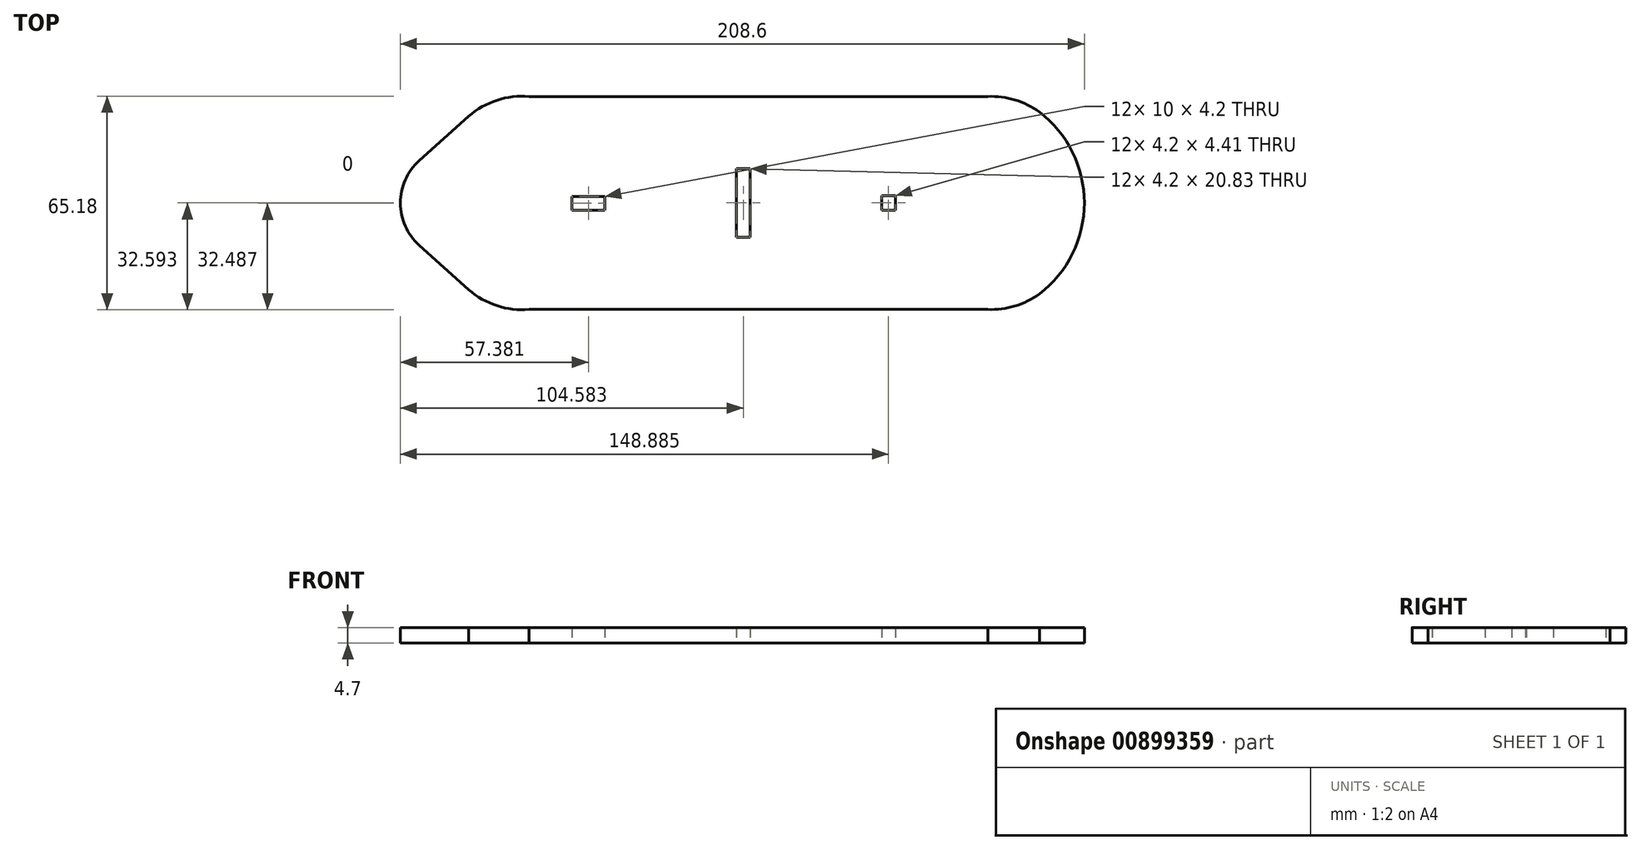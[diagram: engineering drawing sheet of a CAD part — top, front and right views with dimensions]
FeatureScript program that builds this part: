
annotation { "Feature Type Name" : "Feature", "Feature Type Description" : "" }
export const myFeature = defineFeature(function(context is Context, id is Id, definition is map)
    precondition{}
    {
        {
            var Q0;
            Q0=qCreatedBy(makeId("Top.planeOp"),FACE);
            var sketch = newSketch(context, id + "F0", { "sketchPlane" : qUnion([Q0])});
            skArc(sketch, "E0.8", {"start": v(94.32, -610.25) * mm, "mid": v(78.14, -618.43) * mm, "end": v(60.17, -620.91) * mm});
            skLineSegment(sketch, "E0.9", {"start": v(-78.18, -620.91) * mm, "end": v(60.17, -620.91) * mm});
            skPoint(sketch, "E1.middle", {"position": v(-6.1, 79.7) * mm});
            skPoint(sketch, "E2.endSnap0", {"position": v(-81.1, 79.7) * mm});
            skPoint(sketch, "E3", {"position": v(-9.8, 79.7) * mm});
            skPoint(sketch, "E4.orphan", {"position": v(-100.53, 79.7) * mm});
            skPoint(sketch, "E5", {"position": v(-57, 79.6) * mm});
            skPoint(sketch, "E6", {"position": v(34.7, 79.7) * mm});
            skLineSegment(sketch, "E7.bottom", {"start": v(-62, 81.7) * mm, "end": v(-52, 81.7) * mm});
            skLineSegment(sketch, "E7.top", {"start": v(-62, 77.5) * mm, "end": v(-52, 77.5) * mm});
            skLineSegment(sketch, "E7.left", {"start": v(-62, 81.7) * mm, "end": v(-62, 77.5) * mm});
            skLineSegment(sketch, "E7.right", {"start": v(-52, 81.7) * mm, "end": v(-52, 77.5) * mm});
            skLineSegment(sketch, "E8.MirrorCS", {"start": v(32.4, 81.9) * mm, "end": v(32.4, 77.5) * mm});
            skLineSegment(sketch, "E9.MirrorCS", {"start": v(36.6, 81.9) * mm, "end": v(32.4, 81.9) * mm});
            skLineSegment(sketch, "E10.MirrorCS", {"start": v(36.6, 81.9) * mm, "end": v(36.6, 77.5) * mm});
            skLineSegment(sketch, "E11.MirrorCS", {"start": v(36.6, 77.5) * mm, "end": v(32.4, 77.5) * mm});
            skLineSegment(sketch, "E12.bottom", {"start": v(-11.9, 90.12) * mm, "end": v(-7.7, 90.12) * mm});
            skLineSegment(sketch, "E12.top", {"start": v(-11.9, 69.29) * mm, "end": v(-7.7, 69.29) * mm});
            skLineSegment(sketch, "E12.left", {"start": v(-11.9, 90.12) * mm, "end": v(-11.9, 69.29) * mm});
            skLineSegment(sketch, "E12.right", {"start": v(-7.7, 90.12) * mm, "end": v(-7.7, 69.29) * mm});
            skPoint(sketch, "E13.orphan", {"position": v(-81.1, 97.2) * mm});
            skArc(sketch, "E14.4", {"start": v(74.6, 99.4) * mm, "mid": v(74.57, 99.43) * mm, "end": v(74.54, 99.45) * mm});
            skArc(sketch, "E15.0", {"start": v(-75.1, 112.2) * mm, "mid": v(-84.95, 111.06) * mm, "end": v(-93.57, 106.16) * mm});
            skLineSegment(sketch, "E15.1", {"start": v(-93.57, 106.16) * mm, "end": v(-108.66, 92.57) * mm});
            skLineSegment(sketch, "E15.2", {"start": v(-75.1, 112.2) * mm, "end": v(64.79, 112.2) * mm});
            skArc(sketch, "E15.3", {"start": v(-108.66, 92.57) * mm, "mid": v(-114.39, 79.7) * mm, "end": v(-108.66, 66.84) * mm});
            skLineSegment(sketch, "E15.4", {"start": v(-108.66, 66.84) * mm, "end": v(-93.57, 53.25) * mm});
            skArc(sketch, "E15.5", {"start": v(-75.1, 47.2) * mm, "mid": v(-84.95, 48.35) * mm, "end": v(-93.57, 53.25) * mm});
            skArc(sketch, "E15.6", {"start": v(80.5, 107.48) * mm, "mid": v(73.04, 111.17) * mm, "end": v(64.79, 112.2) * mm});
            skArc(sketch, "E15.7", {"start": v(80.5, 51.93) * mm, "mid": v(94.21, 79.7) * mm, "end": v(80.5, 107.48) * mm});
            skArc(sketch, "E15.8", {"start": v(80.5, 51.93) * mm, "mid": v(73.04, 48.24) * mm, "end": v(64.79, 47.2) * mm});
            skLineSegment(sketch, "E15.9", {"start": v(-75.1, 47.2) * mm, "end": v(64.79, 47.2) * mm});
            skLineSegment(sketch, "E16.trimOffspring", {"start": v(68.9, 62.66) * mm, "end": v(68.9, 62.2) * mm});
            skPoint(sketch, "E17.orphan", {"position": v(71.56, 63.97) * mm});
            skPoint(sketch, "E18.orphan", {"position": v(71.56, 95.43) * mm});
            skPoint(sketch, "E19.end.orphan", {"position": v(65.17, 97.2) * mm});
            skSolve(sketch);
        }
        {
            var Q0;
            Q0=makeQuery(id+"F0.imprint","IMPRINT",FACE,{"disambiguationData":[TD([[makeQuery(id+"F0.imprint","IMPRINT",EDGE,{"derivedFrom":sQuery(id+"F0.wireOp",EDGE,"E7.bottom")}),1.0]])]});
            extrude(context, id + "F1", {"entities" : qUnion([Q0]), "depth" : 4.7 * mm, "offsetDistance" : 25 * mm});
        }
    });
